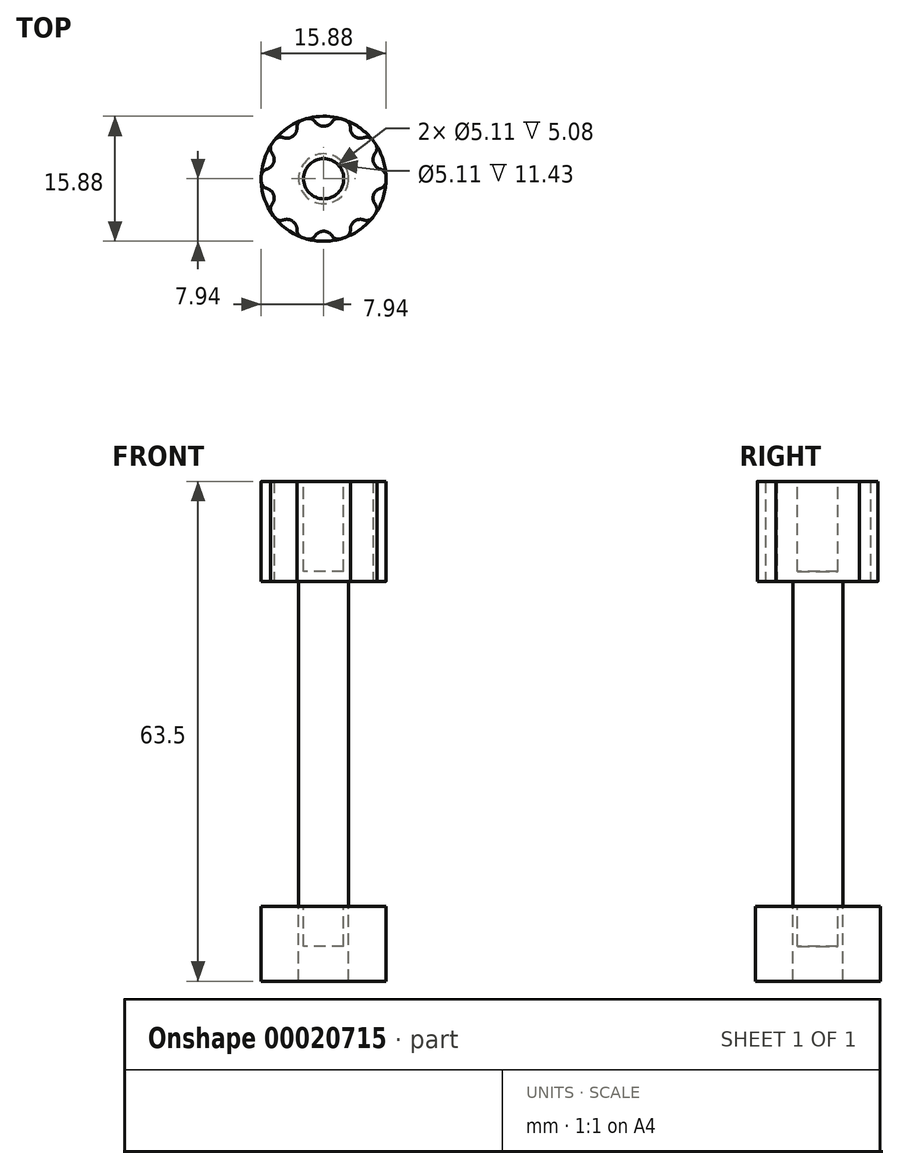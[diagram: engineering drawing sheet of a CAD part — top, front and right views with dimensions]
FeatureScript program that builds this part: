
annotation { "Feature Type Name" : "Feature", "Feature Type Description" : "" }
export const myFeature = defineFeature(function(context is Context, id is Id, definition is map)
    precondition{}
    {
        {
            var Q0;
            Q0=qCreatedBy(makeId("Top.planeOp"),FACE);
            var sketch = newSketch(context, id + "F0", { "sketchPlane" : qUnion([Q0])});
            skCircle(sketch, "E0", {"center": v(0, 0) * mm, "radius": 7.94 * mm});
            skSolve(sketch);
        }
        {
            var Q0;
            Q0 = qSketchRegion(id + "F0", true);
            extrude(context, id + "F1", {"entities" : qUnion([Q0]), "depth" : 12.7 * mm});
        }
        {
            var Q0;
            Q0=makeQuery(id+"F1.opExtrude","CAP_FACE",FACE,{"disambiguationData":[OSD([sQuery(id+"F0.wireOp",EDGE,"E0")])],"isStart":true});
            var sketch = newSketch(context, id + "F2", { "sketchPlane" : qUnion([Q0])});
            skCircle(sketch, "E1", {"center": v(0, 0) * mm, "radius": 3.18 * mm});
            skSolve(sketch);
        }
        {
            var Q0;
            Q0=makeQuery(id+"F2.imprint","IMPRINT",FACE,{"disambiguationData":[TD([[makeQuery(id+"F2.imprint","IMPRINT",EDGE,{"derivedFrom":sQuery(id+"F2.wireOp",EDGE,"E1")}),1.0]])]});
            extrude(context, id + "F3", {"entities" : qUnion([Q0]), "depth" : 50.8 * mm});
        }
        {
            var Q0;
            Q0=makeQuery(id+"F3.opExtrude","CAP_FACE",FACE,{"disambiguationData":[OSD([sQuery(id+"F2.wireOp",EDGE,"E1")])],"isStart":false});
            var sketch = newSketch(context, id + "F4", { "sketchPlane" : qUnion([Q0])});
            skCircle(sketch, "E2", {"center": v(0, 0) * mm, "radius": 7.94 * mm});
            skSolve(sketch);
        }
        {
            var Q0;
            Q0 = qSketchRegion(id + "F4", true);
            extrude(context, id + "F5", {"entities" : qUnion([Q0]), "oppositeDirection" : true, "depth" : 9.52 * mm});
        }
        {
            var Q0;
            Q0=makeQuery(id+"F1.opExtrude","CAP_FACE",FACE,{"disambiguationData":[OSD([sQuery(id+"F0.wireOp",EDGE,"E0")])],"isStart":true});
            var sketch = newSketch(context, id + "F6", { "sketchPlane" : qUnion([Q0])});
            skCircle(sketch, "E3", {"center": v(0, 7.94) * mm, "radius": 1.27 * mm});
            skCircle(sketch, "E4.1.0", {"center": v(-4.67, 6.42) * mm, "radius": 1.27 * mm});
            skCircle(sketch, "E4.2.0", {"center": v(-7.55, 2.45) * mm, "radius": 1.27 * mm});
            skCircle(sketch, "E4.3.0", {"center": v(-7.55, -2.45) * mm, "radius": 1.27 * mm});
            skCircle(sketch, "E4.4.0", {"center": v(-4.67, -6.42) * mm, "radius": 1.27 * mm});
            skCircle(sketch, "E4.5.0", {"center": v(0, -7.94) * mm, "radius": 1.27 * mm});
            skCircle(sketch, "E4.6.0", {"center": v(4.67, -6.42) * mm, "radius": 1.27 * mm});
            skCircle(sketch, "E4.7.0", {"center": v(7.55, -2.45) * mm, "radius": 1.27 * mm});
            skCircle(sketch, "E4.8.0", {"center": v(7.55, 2.45) * mm, "radius": 1.27 * mm});
            skCircle(sketch, "E4.9.0", {"center": v(4.67, 6.42) * mm, "radius": 1.27 * mm});
            skPoint(sketch, "E4.center", {"position": v(0, 0) * mm});
            skSolve(sketch);
        }
        {
            var Q0;
            Q0 = qSketchRegion(id + "F6", true);
            extrude(context, id + "F7", {"entities" : qUnion([Q0]), "operationType" : NewBodyOperationType.REMOVE, "oppositeDirection" : true, "depth" : 25.4 * mm});
        }
        {
            var Q0;
            Q0=makeQuery(id+"F1.opExtrude","CAP_FACE",FACE,{"disambiguationData":[OSD([sQuery(id+"F0.wireOp",EDGE,"E0")])],"isStart":false});
            var sketch = newSketch(context, id + "F8", { "sketchPlane" : qUnion([Q0])});
            skCircle(sketch, "E5", {"center": v(0, 0) * mm, "radius": 2.55 * mm});
            skSolve(sketch);
        }
        {
            var Q0;
            Q0=makeQuery(id+"F8.imprint","IMPRINT",FACE,{"disambiguationData":[TD([[makeQuery(id+"F8.imprint","IMPRINT",EDGE,{"derivedFrom":sQuery(id+"F8.wireOp",EDGE,"E5")}),1.0]])]});
            extrude(context, id + "F9", {"entities" : qUnion([Q0]), "operationType" : NewBodyOperationType.REMOVE, "oppositeDirection" : true, "depth" : 11.43 * mm});
        }
        {
            var Q0;
            Q0=makeQuery(id+"F7.boolean.opBoolean","INTERSECT",EDGE,{"disambiguationData":[OD(0.0)],"derivedFrom":[makeQuery(id+"F1.opExtrude","SWEPT_FACE",FACE,{"disambiguationData":[OSD([sQuery(id+"F0.wireOp",EDGE,"E0")])]}),makeQuery(id+"F7.opExtrude","SWEPT_FACE",FACE,{"disambiguationData":[OSD([sQuery(id+"F6.wireOp",EDGE,"E4.5.0")])]})]});
            var Q1;
            Q1=makeQuery(id+"F7.boolean.opBoolean","INTERSECT",EDGE,{"disambiguationData":[OD(1.0)],"derivedFrom":[makeQuery(id+"F1.opExtrude","SWEPT_FACE",FACE,{"disambiguationData":[OSD([sQuery(id+"F0.wireOp",EDGE,"E0")])]}),makeQuery(id+"F7.opExtrude","SWEPT_FACE",FACE,{"disambiguationData":[OSD([sQuery(id+"F6.wireOp",EDGE,"E4.5.0")])]})]});
            var Q2;
            Q2=makeQuery(id+"F7.boolean.opBoolean","INTERSECT",EDGE,{"disambiguationData":[OD(0.0)],"derivedFrom":[makeQuery(id+"F1.opExtrude","SWEPT_FACE",FACE,{"disambiguationData":[OSD([sQuery(id+"F0.wireOp",EDGE,"E0")])]}),makeQuery(id+"F7.opExtrude","SWEPT_FACE",FACE,{"disambiguationData":[OSD([sQuery(id+"F6.wireOp",EDGE,"E4.6.0")])]})]});
            var Q3;
            Q3=makeQuery(id+"F7.boolean.opBoolean","INTERSECT",EDGE,{"disambiguationData":[OD(1.0)],"derivedFrom":[makeQuery(id+"F1.opExtrude","SWEPT_FACE",FACE,{"disambiguationData":[OSD([sQuery(id+"F0.wireOp",EDGE,"E0")])]}),makeQuery(id+"F7.opExtrude","SWEPT_FACE",FACE,{"disambiguationData":[OSD([sQuery(id+"F6.wireOp",EDGE,"E4.6.0")])]})]});
            var Q4;
            Q4=makeQuery(id+"F7.boolean.opBoolean","INTERSECT",EDGE,{"disambiguationData":[OD(0.0)],"derivedFrom":[makeQuery(id+"F1.opExtrude","SWEPT_FACE",FACE,{"disambiguationData":[OSD([sQuery(id+"F0.wireOp",EDGE,"E0")])]}),makeQuery(id+"F7.opExtrude","SWEPT_FACE",FACE,{"disambiguationData":[OSD([sQuery(id+"F6.wireOp",EDGE,"E4.7.0")])]})]});
            var Q5;
            Q5=makeQuery(id+"F7.boolean.opBoolean","INTERSECT",EDGE,{"disambiguationData":[OD(1.0)],"derivedFrom":[makeQuery(id+"F1.opExtrude","SWEPT_FACE",FACE,{"disambiguationData":[OSD([sQuery(id+"F0.wireOp",EDGE,"E0")])]}),makeQuery(id+"F7.opExtrude","SWEPT_FACE",FACE,{"disambiguationData":[OSD([sQuery(id+"F6.wireOp",EDGE,"E4.7.0")])]})]});
            var Q6;
            Q6=makeQuery(id+"F7.boolean.opBoolean","INTERSECT",EDGE,{"disambiguationData":[OD(0.0)],"derivedFrom":[makeQuery(id+"F1.opExtrude","SWEPT_FACE",FACE,{"disambiguationData":[OSD([sQuery(id+"F0.wireOp",EDGE,"E0")])]}),makeQuery(id+"F7.opExtrude","SWEPT_FACE",FACE,{"disambiguationData":[OSD([sQuery(id+"F6.wireOp",EDGE,"E4.8.0")])]})]});
            var Q7;
            Q7=makeQuery(id+"F7.boolean.opBoolean","INTERSECT",EDGE,{"disambiguationData":[OD(1.0)],"derivedFrom":[makeQuery(id+"F1.opExtrude","SWEPT_FACE",FACE,{"disambiguationData":[OSD([sQuery(id+"F0.wireOp",EDGE,"E0")])]}),makeQuery(id+"F7.opExtrude","SWEPT_FACE",FACE,{"disambiguationData":[OSD([sQuery(id+"F6.wireOp",EDGE,"E4.8.0")])]})]});
            var Q8;
            Q8=makeQuery(id+"F7.boolean.opBoolean","INTERSECT",EDGE,{"disambiguationData":[OD(0.0)],"derivedFrom":[makeQuery(id+"F1.opExtrude","SWEPT_FACE",FACE,{"disambiguationData":[OSD([sQuery(id+"F0.wireOp",EDGE,"E0")])]}),makeQuery(id+"F7.opExtrude","SWEPT_FACE",FACE,{"disambiguationData":[OSD([sQuery(id+"F6.wireOp",EDGE,"E4.9.0")])]})]});
            var Q9;
            Q9=makeQuery(id+"F7.boolean.opBoolean","INTERSECT",EDGE,{"disambiguationData":[OD(1.0)],"derivedFrom":[makeQuery(id+"F1.opExtrude","SWEPT_FACE",FACE,{"disambiguationData":[OSD([sQuery(id+"F0.wireOp",EDGE,"E0")])]}),makeQuery(id+"F7.opExtrude","SWEPT_FACE",FACE,{"disambiguationData":[OSD([sQuery(id+"F6.wireOp",EDGE,"E3")])]})]});
            var Q10;
            Q10=makeQuery(id+"F7.boolean.opBoolean","INTERSECT",EDGE,{"disambiguationData":[OD(0.0)],"derivedFrom":[makeQuery(id+"F1.opExtrude","SWEPT_FACE",FACE,{"disambiguationData":[OSD([sQuery(id+"F0.wireOp",EDGE,"E0")])]}),makeQuery(id+"F7.opExtrude","SWEPT_FACE",FACE,{"disambiguationData":[OSD([sQuery(id+"F6.wireOp",EDGE,"E3")])]})]});
            var Q11;
            Q11=makeQuery(id+"F7.boolean.opBoolean","INTERSECT",EDGE,{"disambiguationData":[OD(0.0)],"derivedFrom":[makeQuery(id+"F1.opExtrude","SWEPT_FACE",FACE,{"disambiguationData":[OSD([sQuery(id+"F0.wireOp",EDGE,"E0")])]}),makeQuery(id+"F7.opExtrude","SWEPT_FACE",FACE,{"disambiguationData":[OSD([sQuery(id+"F6.wireOp",EDGE,"E4.1.0")])]})]});
            var Q12;
            Q12=makeQuery(id+"F7.boolean.opBoolean","INTERSECT",EDGE,{"disambiguationData":[OD(1.0)],"derivedFrom":[makeQuery(id+"F1.opExtrude","SWEPT_FACE",FACE,{"disambiguationData":[OSD([sQuery(id+"F0.wireOp",EDGE,"E0")])]}),makeQuery(id+"F7.opExtrude","SWEPT_FACE",FACE,{"disambiguationData":[OSD([sQuery(id+"F6.wireOp",EDGE,"E4.1.0")])]})]});
            var Q13;
            Q13=makeQuery(id+"F7.boolean.opBoolean","INTERSECT",EDGE,{"disambiguationData":[OD(0.0)],"derivedFrom":[makeQuery(id+"F1.opExtrude","SWEPT_FACE",FACE,{"disambiguationData":[OSD([sQuery(id+"F0.wireOp",EDGE,"E0")])]}),makeQuery(id+"F7.opExtrude","SWEPT_FACE",FACE,{"disambiguationData":[OSD([sQuery(id+"F6.wireOp",EDGE,"E4.2.0")])]})]});
            var Q14;
            Q14=makeQuery(id+"F7.boolean.opBoolean","INTERSECT",EDGE,{"disambiguationData":[OD(1.0)],"derivedFrom":[makeQuery(id+"F1.opExtrude","SWEPT_FACE",FACE,{"disambiguationData":[OSD([sQuery(id+"F0.wireOp",EDGE,"E0")])]}),makeQuery(id+"F7.opExtrude","SWEPT_FACE",FACE,{"disambiguationData":[OSD([sQuery(id+"F6.wireOp",EDGE,"E4.2.0")])]})]});
            var Q15;
            Q15=makeQuery(id+"F7.boolean.opBoolean","INTERSECT",EDGE,{"disambiguationData":[OD(0.0)],"derivedFrom":[makeQuery(id+"F1.opExtrude","SWEPT_FACE",FACE,{"disambiguationData":[OSD([sQuery(id+"F0.wireOp",EDGE,"E0")])]}),makeQuery(id+"F7.opExtrude","SWEPT_FACE",FACE,{"disambiguationData":[OSD([sQuery(id+"F6.wireOp",EDGE,"E4.3.0")])]})]});
            var Q16;
            Q16=makeQuery(id+"F7.boolean.opBoolean","INTERSECT",EDGE,{"disambiguationData":[OD(1.0)],"derivedFrom":[makeQuery(id+"F1.opExtrude","SWEPT_FACE",FACE,{"disambiguationData":[OSD([sQuery(id+"F0.wireOp",EDGE,"E0")])]}),makeQuery(id+"F7.opExtrude","SWEPT_FACE",FACE,{"disambiguationData":[OSD([sQuery(id+"F6.wireOp",EDGE,"E4.3.0")])]})]});
            var Q17;
            Q17=makeQuery(id+"F7.boolean.opBoolean","INTERSECT",EDGE,{"disambiguationData":[OD(0.0)],"derivedFrom":[makeQuery(id+"F1.opExtrude","SWEPT_FACE",FACE,{"disambiguationData":[OSD([sQuery(id+"F0.wireOp",EDGE,"E0")])]}),makeQuery(id+"F7.opExtrude","SWEPT_FACE",FACE,{"disambiguationData":[OSD([sQuery(id+"F6.wireOp",EDGE,"E4.4.0")])]})]});
            var Q18;
            Q18=makeQuery(id+"F7.boolean.opBoolean","INTERSECT",EDGE,{"disambiguationData":[OD(1.0)],"derivedFrom":[makeQuery(id+"F1.opExtrude","SWEPT_FACE",FACE,{"disambiguationData":[OSD([sQuery(id+"F0.wireOp",EDGE,"E0")])]}),makeQuery(id+"F7.opExtrude","SWEPT_FACE",FACE,{"disambiguationData":[OSD([sQuery(id+"F6.wireOp",EDGE,"E4.9.0")])]})]});
            var Q19;
            Q19=makeQuery(id+"F7.boolean.opBoolean","INTERSECT",EDGE,{"disambiguationData":[OD(1.0)],"derivedFrom":[makeQuery(id+"F1.opExtrude","SWEPT_FACE",FACE,{"disambiguationData":[OSD([sQuery(id+"F0.wireOp",EDGE,"E0")])]}),makeQuery(id+"F7.opExtrude","SWEPT_FACE",FACE,{"disambiguationData":[OSD([sQuery(id+"F6.wireOp",EDGE,"E4.4.0")])]})]});
            fillet(context, id + "F10", {"entities" : qUnion([Q0, Q1, Q2, Q3, Q4, Q5, Q6, Q7, Q8, Q9, Q10, Q11, Q12, Q13, Q14, Q15, Q16, Q17, Q18, Q19]), "radius" : 1.02 * mm, "tangentPropagation" : true, "allowEdgeOverflow" : false});
        }
        {
            var Q0;
            Q0=makeQuery(id+"F5.opExtrude","CAP_FACE",FACE,{"disambiguationData":[OSD([sQuery(id+"F4.wireOp",EDGE,"E2")])],"isStart":false});
            var sketch = newSketch(context, id + "F11", { "sketchPlane" : qUnion([Q0])});
            skCircle(sketch, "E6", {"center": v(0, 0) * mm, "radius": 2.55 * mm});
            skSolve(sketch);
        }
        {
            var Q0;
            Q0 = qSketchRegion(id + "F11", true);
            extrude(context, id + "F12", {"entities" : qUnion([Q0]), "operationType" : NewBodyOperationType.REMOVE, "oppositeDirection" : true, "depth" : 5.08 * mm});
        }
    });
